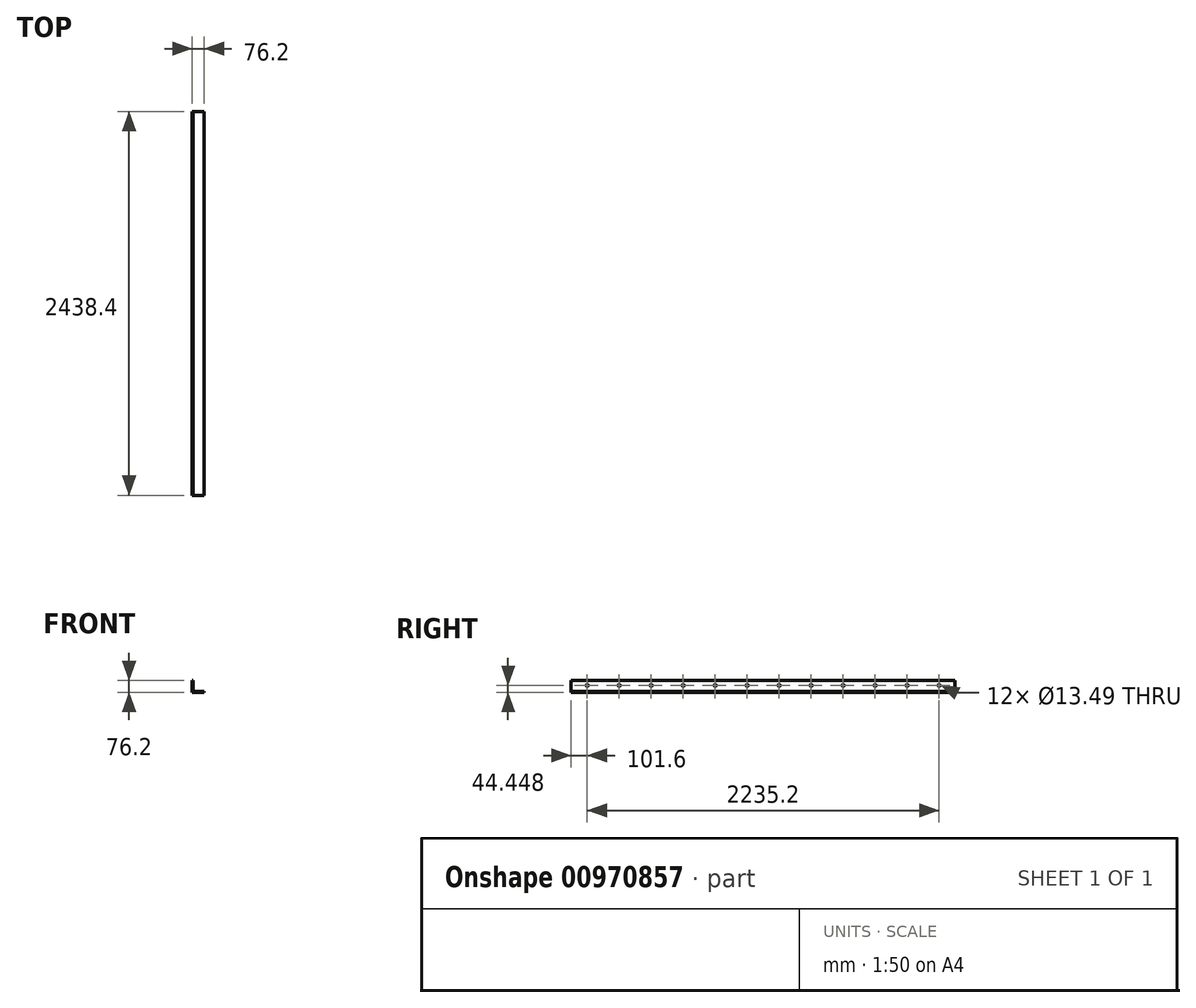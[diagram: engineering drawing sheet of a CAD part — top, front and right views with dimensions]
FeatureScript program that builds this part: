
annotation { "Feature Type Name" : "Feature", "Feature Type Description" : "" }
export const myFeature = defineFeature(function(context is Context, id is Id, definition is map)
    precondition{}
    {
        {
            var Q0;
            Q0=qCreatedBy(makeId("Front.planeOp"),FACE);
            var sketch = newSketch(context, id + "F0", { "sketchPlane" : qUnion([Q0])});
            skLineSegment(sketch, "E0", {"start": v(-63.67, 46.35) * mm, "end": v(-63.67, -29.85) * mm});
            skLineSegment(sketch, "E1", {"start": v(-63.67, -29.85) * mm, "end": v(12.53, -29.85) * mm});
            skLineSegment(sketch, "E2", {"start": v(12.53, -29.85) * mm, "end": v(12.53, -23.5) * mm});
            skLineSegment(sketch, "E3", {"start": v(12.53, -23.5) * mm, "end": v(-57.32, -23.5) * mm});
            skLineSegment(sketch, "E4", {"start": v(-57.32, -23.5) * mm, "end": v(-57.32, 46.35) * mm});
            skLineSegment(sketch, "E5", {"start": v(-57.32, 46.35) * mm, "end": v(-63.67, 46.35) * mm});
            skSolve(sketch);
        }
        {
            var Q0;
            Q0=makeQuery(id+"F0.imprint","IMPRINT",FACE,{"disambiguationData":[TD([[makeQuery(id+"F0.imprint","IMPRINT",EDGE,{"derivedFrom":sQuery(id+"F0.wireOp",EDGE,"E0")}),1.0]])]});
            extrude(context, id + "F1", {"entities" : qUnion([Q0]), "depth" : 2438.4 * mm, "offsetDistance" : 25.4 * mm});
        }
        {
            var Q0;
            Q0=makeQuery(id+"F1.opExtrude","SWEPT_FACE",FACE,{"disambiguationData":[OSD([sQuery(id+"F0.wireOp",EDGE,"E0")])]});
            var sketch = newSketch(context, id + "F2", { "sketchPlane" : qUnion([Q0])});
            skCircle(sketch, "E6", {"center": v(2336.8, 14.6) * mm, "radius": 6.74 * mm});
            skCircle(sketch, "E7", {"center": v(2438.4, 20.98) * mm, "radius": 2.17 * mm});
            skCircle(sketch, "E8.1.0.0", {"center": v(2133.6, 14.6) * mm, "radius": 6.74 * mm});
            skCircle(sketch, "E8.2.0.0", {"center": v(1930.4, 14.6) * mm, "radius": 6.74 * mm});
            skCircle(sketch, "E8.3.0.0", {"center": v(1727.2, 14.6) * mm, "radius": 6.74 * mm});
            skCircle(sketch, "E8.4.0.0", {"center": v(1524, 14.6) * mm, "radius": 6.74 * mm});
            skCircle(sketch, "E8.5.0.0", {"center": v(1320.8, 14.6) * mm, "radius": 6.74 * mm});
            skCircle(sketch, "E8.6.0.0", {"center": v(1117.6, 14.6) * mm, "radius": 6.74 * mm});
            skCircle(sketch, "E8.7.0.0", {"center": v(914.4, 14.6) * mm, "radius": 6.74 * mm});
            skCircle(sketch, "E8.8.0.0", {"center": v(711.2, 14.6) * mm, "radius": 6.74 * mm});
            skCircle(sketch, "E8.9.0.0", {"center": v(508, 14.6) * mm, "radius": 6.74 * mm});
            skCircle(sketch, "E8.10.0.0", {"center": v(304.8, 14.6) * mm, "radius": 6.74 * mm});
            skCircle(sketch, "E8.11.0.0", {"center": v(101.6, 14.6) * mm, "radius": 6.74 * mm});
            skLineSegment(sketch, "E8.direction1", {"start": v(2336.8, 14.6) * mm, "end": v(2133.6, 14.6) * mm, "construction": true});
            skSolve(sketch);
        }
        {
            var Q0;
            Q0=sQuery(id+"F2.wireOp",VERTEX,"E8.direction1.start");
            var Q1;
            Q1=sQuery(id+"F2.wireOp",VERTEX,"E8.direction1.end");
            var Q2;
            Q2=sQuery(id+"F2.wireOp",VERTEX,"E8.2.0.0.center");
            var Q3;
            Q3=sQuery(id+"F2.wireOp",VERTEX,"E8.3.0.0.center");
            var Q4;
            Q4=sQuery(id+"F2.wireOp",VERTEX,"E8.4.0.0.center");
            var Q5;
            Q5=sQuery(id+"F2.wireOp",VERTEX,"E8.5.0.0.center");
            var Q6;
            Q6=sQuery(id+"F2.wireOp",VERTEX,"E8.6.0.0.center");
            var Q7;
            Q7=sQuery(id+"F2.wireOp",VERTEX,"E8.7.0.0.center");
            var Q8;
            Q8=sQuery(id+"F2.wireOp",VERTEX,"E8.8.0.0.center");
            var Q9;
            Q9=sQuery(id+"F2.wireOp",VERTEX,"E8.9.0.0.center");
            var Q10;
            Q10=sQuery(id+"F2.wireOp",VERTEX,"E8.10.0.0.center");
            var Q11;
            Q11=sQuery(id+"F2.wireOp",VERTEX,"E8.11.0.0.center");
            var Q12;
            Q12=makeQuery(id+"F1.opExtrude","SWEPT_BODY",BODY,{"disambiguationData":[OSD([sQuery(id+"F0.wireOp",EDGE,"E0"),sQuery(id+"F0.wireOp",EDGE,"E1"),sQuery(id+"F0.wireOp",EDGE,"E2"),sQuery(id+"F0.wireOp",EDGE,"E3"),sQuery(id+"F0.wireOp",EDGE,"E4"),sQuery(id+"F0.wireOp",EDGE,"E5")])]});
            hole(context, id + "F3", {"style" : HoleStyle.SIMPLE, "endStyle" : HoleEndStyle.THROUGH, "holeDiameter" : 13.5 * mm, "majorDiameter" : 6.35 * mm, "isTappedThrough" : true, "tappedDepth" : 12.7 * mm, "tapClearance" : 3, "locations" : qUnion([Q0, Q1, Q2, Q3, Q4, Q5, Q6, Q7, Q8, Q9, Q10, Q11]), "scope" : qUnion([Q12]), "startStyle" : HoleStartStyle.SKETCH});
        }
    });
